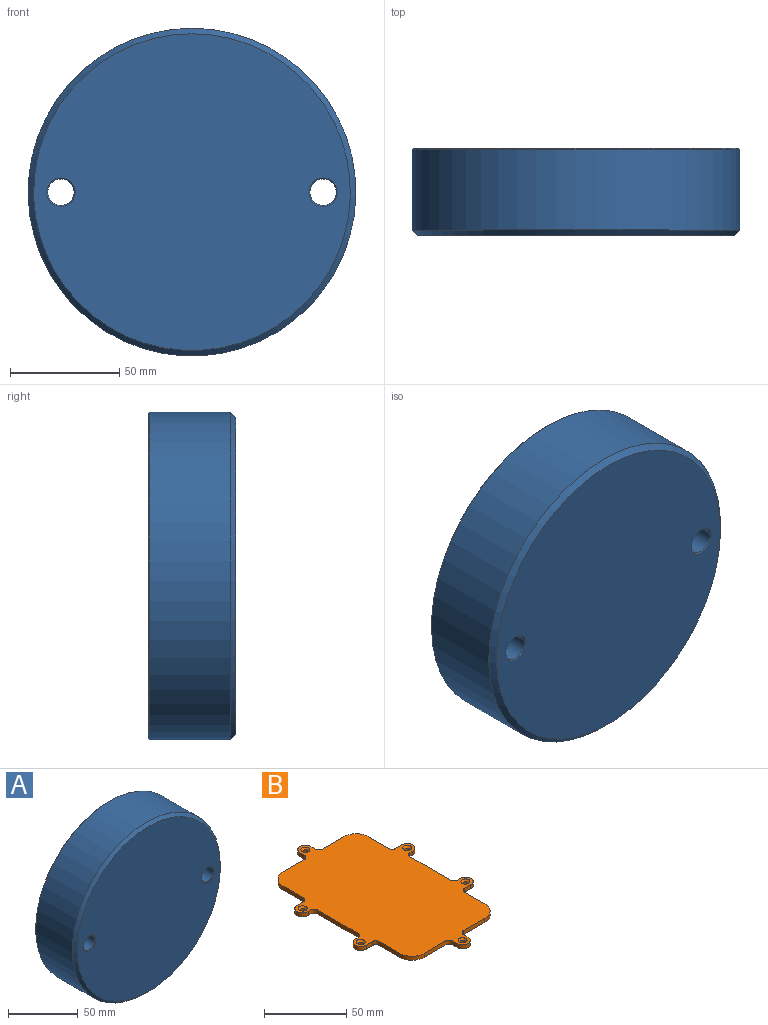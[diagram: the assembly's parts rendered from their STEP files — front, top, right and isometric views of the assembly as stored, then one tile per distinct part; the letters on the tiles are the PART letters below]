
ASSEMBLY  parts=2 mates=1
PART A: 111 faces, bbox 150x40x150 mm
  f0: cone r=75mm half-angle=45deg, axis (0,1,0), area 1638.3mm2, adj f15,f22
  f1: cone r=6mm half-angle=45deg, axis (0,1,0), area 27.8mm2, adj f13,f21
  f2: cone r=6mm half-angle=45deg, axis (0,1,0), area 27.8mm2, adj f14,f21
  f3: cone r=6mm half-angle=45deg, axis (0,-1,0), area 27.8mm2, adj f14,f22
  f4: cone r=6mm half-angle=45deg, axis (0,-1,0), area 27.8mm2, adj f13,f22
  f5: cone r=74.5mm half-angle=45deg, axis (0,-1,0), area 332.1mm2, adj f15,f21
  f6: cylinder r=1.5mm len=16mm, axis (0,1,0), area 150.8mm2, adj f16,f110
  f7: cylinder r=1.5mm len=16mm, axis (0,1,0), area 150.8mm2, adj f17,f109
  f8: cylinder r=1.5mm len=16mm, axis (0,1,0), area 150.8mm2, adj f18,f108
  f9: cylinder r=1.5mm len=16mm, axis (0,1,0), area 150.8mm2, adj f19,f107
  f10: cylinder r=1.5mm len=16mm, axis (0,1,0), area 150.8mm2, adj f20,f106
  f11: cylinder r=1.5mm len=16mm, axis (0,1,0), area 150.8mm2, adj f20,f105
  f12: cylinder r=5mm len=10mm, axis (0,1,0), area 47.1mm2, adj f16,f21,f46,f47
  f13: cylinder r=6mm len=39mm, axis (0,1,0), area 1470.3mm2, adj f1,f4
  f14: cylinder r=6mm len=39mm, axis (0,1,0), area 1470.3mm2, adj f2,f3
  f15: cylinder r=75mm len=150mm, axis (0,-1,0), area 17435.8mm2, adj f0,f5
  f16: plane 15x11.5mm, normal (0,1,0), area 99.9mm2, adj f6,f12,f44,f45,f46,f47,f48
  f17: plane 12.71x11.5mm, normal (0,1,0), area 84.3mm2, adj f7,f51,f52,f53,f54,f55,f56,f79
  f18: plane 15x11.5mm, normal (0,1,0), area 99.9mm2, adj f8,f23,f24,f25,f26,f27,f28
  f19: plane 12.71x11.5mm, normal (0,1,0), area 84.3mm2, adj f9,f56,f57,f58,f59,f60,f61,f80
  f20: plane 62.71x13mm, normal (0,1,0), area 169.1mm2, adj f10,f11,f31,f32,f33,f34,f35,f36
  f21: plane 149x149mm, normal (0,1,0), area 7305.3mm2, adj f1,f2,f5,f12,f23,f24,f25,f26
  f22: plane 145x145mm, normal (0,-1,0), area 16247.5mm2, adj f0,f3,f4
  f23: cylinder r=2.5mm len=3mm, axis (0,1,0), area 11.8mm2, adj f18,f21,f24,f28
  f24: plane 4x3mm, normal (1,0,0), area 12mm2, adj f18,f21,f23,f25
  f25: cylinder r=5mm len=10mm, axis (0,1,0), area 47.1mm2, adj f18,f21,f24,f26
  f26: plane 4x3mm, normal (-1,0,0), area 12mm2, adj f18,f21,f25,f27
  f27: cylinder r=2.5mm len=3mm, axis (0,1,0), area 11.8mm2, adj f18,f21,f26,f28
  f28: plane 52x6mm, normal (0,0,1), area 267mm2, adj f18,f21,f23,f27,f29,f63,f86
  f29: cylinder r=11mm len=11mm, axis (0,1,0), area 103.7mm2, adj f21,f28,f30,f86
  f30: plane 17.5x6mm, normal (-1,0,0), area 105mm2, adj f21,f29,f31,f81,f86
  f31: cylinder r=2.5mm len=3mm, axis (0,1,0), area 11.8mm2, adj f20,f21,f30,f32
  f32: plane 5.5x3mm, normal (0,0,1), area 16.5mm2, adj f20,f21,f31,f33
  f33: cylinder r=5mm len=10mm, axis (0,1,0), area 47.1mm2, adj f20,f21,f32,f34
  f34: plane 3x2.5mm, normal (0,0,-1), area 7.5mm2, adj f20,f21,f33,f35
  f35: cylinder r=2.5mm len=3mm, axis (0,1,0), area 11.8mm2, adj f20,f21,f34,f36
  f36: plane 35x3mm, normal (-1,0,0), area 105mm2, adj f20,f21,f35,f37
  f37: cylinder r=2.5mm len=3mm, axis (0,1,0), area 11.8mm2, adj f20,f21,f36,f38
  f38: plane 3x2.5mm, normal (0,0,1), area 7.5mm2, adj f20,f21,f37,f39
  f39: cylinder r=5mm len=10mm, axis (0,1,0), area 47.1mm2, adj f20,f21,f38,f40
  f40: plane 5.5x3mm, normal (0,0,-1), area 16.5mm2, adj f20,f21,f39,f41
  f41: cylinder r=2.5mm len=6mm, axis (0,1,0), area 20.5mm2, adj f20,f21,f40,f42,f84,f86
  f42: plane 17.5x6mm, normal (-1,0,0), area 105mm2, adj f21,f41,f43,f86
  f43: cylinder r=11mm len=11mm, axis (0,1,0), area 103.7mm2, adj f21,f42,f44,f86
  f44: plane 52x6mm, normal (0,0,-1), area 267mm2, adj f16,f21,f43,f45,f48,f49,f86
  f45: cylinder r=2.5mm len=3mm, axis (0,1,0), area 11.8mm2, adj f16,f21,f44,f46
  f46: plane 4x3mm, normal (-1,0,0), area 12mm2, adj f12,f16,f21,f45
  f47: plane 4x3mm, normal (1,0,0), area 12mm2, adj f12,f16,f21,f48
  f48: cylinder r=2.5mm len=3mm, axis (0,1,0), area 11.8mm2, adj f16,f21,f44,f47
  f49: cylinder r=11mm len=11mm, axis (0,1,0), area 103.7mm2, adj f21,f44,f50,f86
  f50: plane 17.5x6mm, normal (1,0,0), area 105mm2, adj f21,f49,f51,f86
  f51: cylinder r=2.5mm len=6mm, axis (0,1,0), area 20.5mm2, adj f17,f21,f50,f52,f79,f86
  f52: plane 5.5x3mm, normal (0,0,-1), area 16.5mm2, adj f17,f21,f51,f53
  f53: cylinder r=5mm len=10mm, axis (0,1,0), area 47.1mm2, adj f17,f21,f52,f54
  f54: plane 3x2.5mm, normal (0,0,1), area 7.5mm2, adj f17,f21,f53,f55
  f55: cylinder r=2.5mm len=3mm, axis (0,1,0), area 11.8mm2, adj f17,f21,f54,f56
  f56: plane 55.84x6mm, normal (1,0,0), area 272.5mm2, adj f17,f19,f21,f55,f57,f79,f80,f86
  f57: cylinder r=2.5mm len=3mm, axis (0,1,0), area 11.8mm2, adj f19,f21,f56,f58
  f58: plane 3x2.5mm, normal (0,0,-1), area 7.5mm2, adj f19,f21,f57,f59
  f59: cylinder r=5mm len=10mm, axis (0,1,0), area 47.1mm2, adj f19,f21,f58,f60
  f60: plane 5.5x3mm, normal (0,0,1), area 16.5mm2, adj f19,f21,f59,f61
  f61: cylinder r=2.5mm len=6mm, axis (0,1,0), area 20.5mm2, adj f19,f21,f60,f62,f80,f86
  f62: plane 17.5x6mm, normal (1,0,0), area 105mm2, adj f21,f61,f63,f86
  f63: cylinder r=11mm len=11mm, axis (0,1,0), area 103.7mm2, adj f21,f28,f62,f86
  f64: plane 52x3mm, normal (0,0,-1), area 156mm2, adj f65,f85,f86,f104
  f65: cylinder r=7mm len=7mm, axis (0,1,0), area 33mm2, adj f64,f66,f86,f104
  f66: plane 17.5x3mm, normal (-1,0,0), area 52.5mm2, adj f65,f67,f86,f104
  f67: cylinder r=6.5mm len=5.48mm, axis (0,1,0), area 19.5mm2, adj f66,f68,f86,f104
  f68: plane 54.05x3mm, normal (-1,0,0), area 162.1mm2, adj f67,f69,f86,f104
  f69: cylinder r=6.5mm len=5.48mm, axis (0,1,0), area 19.5mm2, adj f68,f70,f86,f104
  f70: plane 17.5x3mm, normal (-1,0,0), area 52.5mm2, adj f69,f71,f86,f104
  f71: cylinder r=7mm len=7mm, axis (0,1,0), area 33mm2, adj f70,f72,f86,f104
  f72: plane 52x3mm, normal (0,0,1), area 156mm2, adj f71,f73,f86,f104
  f73: cylinder r=7mm len=7mm, axis (0,1,0), area 33mm2, adj f72,f74,f86,f104
  f74: plane 17.5x3mm, normal (1,0,0), area 52.5mm2, adj f73,f75,f86,f104
  f75: cylinder r=6.5mm len=5.47mm, axis (0,1,0), area 19.5mm2, adj f74,f76,f86,f104
  f76: plane 54.05x3mm, normal (1,0,0), area 162.2mm2, adj f75,f77,f86,f104
  f77: cylinder r=6.5mm len=5.47mm, axis (0,1,0), area 19.5mm2, adj f76,f78,f86,f104
  f78: plane 17.5x3mm, normal (1,0,0), area 52.5mm2, adj f77,f85,f86,f104
  f79: cylinder r=2.5mm len=3mm, axis (0,1,0), area 8.7mm2, adj f17,f51,f56,f86
  f80: cylinder r=2.5mm len=3mm, axis (0,1,0), area 8.7mm2, adj f19,f56,f61,f86
  f81: cylinder r=2.5mm len=3mm, axis (0,1,0), area 8.7mm2, adj f20,f30,f82,f86
  f82: cylinder r=2.5mm len=3mm, axis (0,1,0), area 8.7mm2, adj f20,f81,f83,f86
  f83: plane 55.84x3mm, normal (-1,0,0), area 167.5mm2, adj f20,f82,f84,f86
  f84: cylinder r=2.5mm len=3mm, axis (0,1,0), area 8.7mm2, adj f20,f41,f83,f86
  f85: cylinder r=7mm len=7mm, axis (0,1,0), area 33mm2, adj f64,f78,f86,f104
  f86: plane 122x79.99mm, normal (0,1,0), area 1461mm2, adj f28,f29,f30,f41,f42,f43,f44,f49
  f87: plane 110x68mm, normal (0,1,0), area 7072.2mm2, adj f88,f89,f90,f91,f92,f93,f94,f95
  f88: cylinder r=5mm len=34mm, axis (0,1,0), area 267mm2, adj f87,f89,f103,f104
  f89: plane 34x25.92mm, normal (-1,0,0), area 881.2mm2, adj f87,f88,f90,f104
  f90: cylinder r=5mm len=34mm, axis (0,1,0), area 197.1mm2, adj f87,f89,f91,f104
  f91: plane 39x34mm, normal (-1,0,0), area 1326mm2, adj f87,f90,f92,f104
  f92: cylinder r=5mm len=34mm, axis (0,1,0), area 197.1mm2, adj f87,f91,f93,f104
  f93: plane 34x25.92mm, normal (-1,0,0), area 881.2mm2, adj f87,f92,f94,f104
  f94: cylinder r=5mm len=34mm, axis (0,1,0), area 267mm2, adj f87,f93,f95,f104
  f95: plane 52x34mm, normal (0,0,1), area 1768mm2, adj f87,f94,f96,f104
  f96: cylinder r=5mm len=34mm, axis (0,1,0), area 267mm2, adj f87,f95,f97,f104
  f97: plane 34x25.92mm, normal (1,0,0), area 881.2mm2, adj f87,f96,f98,f104
  f98: cylinder r=5mm len=34mm, axis (0,1,0), area 197.1mm2, adj f87,f97,f99,f104
  f99: plane 39x34mm, normal (1,0,0), area 1326mm2, adj f87,f98,f100,f104
  f100: cylinder r=5mm len=34mm, axis (0,1,0), area 197.1mm2, adj f87,f99,f101,f104
  f101: plane 34x25.92mm, normal (1,0,0), area 881.2mm2, adj f87,f100,f102,f104
  f102: cylinder r=5mm len=34mm, axis (0,1,0), area 267mm2, adj f87,f101,f103,f104
  f103: plane 52x34mm, normal (0,0,-1), area 1768mm2, adj f87,f88,f102,f104
  f104: plane 114x71.99mm, normal (0,1,0), area 752.8mm2, adj f64,f65,f66,f67,f68,f69,f70,f71
  f105: plane 3x3mm, normal (0,1,0), area 7.1mm2, adj f11
  f106: plane 3x3mm, normal (0,1,0), area 7.1mm2, adj f10
  f107: plane 3x3mm, normal (0,1,0), area 7.1mm2, adj f9
  f108: plane 3x3mm, normal (0,1,0), area 7.1mm2, adj f8
  f109: plane 3x3mm, normal (0,1,0), area 7.1mm2, adj f7
  f110: plane 3x3mm, normal (0,1,0), area 7.1mm2, adj f6
PART B: 58 faces, bbox 99.4x144.4x3 mm
  f0: cone r=2.75mm half-angle=45deg, axis (0,0,1), area 23.6mm2, adj f8,f14
  f1: cone r=2.75mm half-angle=45deg, axis (0,0,1), area 23.6mm2, adj f7,f14
  f2: cone r=2.75mm half-angle=45deg, axis (0,0,1), area 23.6mm2, adj f6,f14
  f3: cone r=2.75mm half-angle=45deg, axis (0,0,1), area 23.6mm2, adj f11,f14
  f4: cone r=2.75mm half-angle=45deg, axis (0,0,1), area 23.6mm2, adj f10,f14
  f5: cone r=2.75mm half-angle=45deg, axis (0,0,1), area 23.6mm2, adj f9,f14
  f6: cylinder r=1.5mm len=3mm, axis (0,0,-1), area 16.5mm2, adj f2,f15
  f7: cylinder r=1.5mm len=3mm, axis (0,0,-1), area 16.5mm2, adj f1,f15
  f8: cylinder r=1.5mm len=3mm, axis (0,0,-1), area 16.5mm2, adj f0,f15
  f9: cylinder r=1.5mm len=3mm, axis (0,0,-1), area 16.5mm2, adj f5,f15
  f10: cylinder r=1.5mm len=3mm, axis (0,0,-1), area 16.5mm2, adj f4,f15
  f11: cylinder r=1.5mm len=3mm, axis (0,0,-1), area 16.5mm2, adj f3,f15
  f12: cylinder r=4.7mm len=9.4mm, axis (0,0,-1), area 44.3mm2, adj f14,f15,f26,f27
  f13: cylinder r=4.7mm len=9.4mm, axis (0,0,-1), area 44.3mm2, adj f14,f15,f21,f22
  f14: plane 144.4x99.4mm, normal (0,0,1), area 9581.8mm2, adj f0,f1,f2,f3,f4,f5,f12,f13
  f15: plane 144.4x99.4mm, normal (0,0,-1), area 9682mm2, adj f6,f7,f8,f9,f10,f11,f12,f13
  f16: cylinder r=2.8mm len=3mm, axis (0,0,-1), area 13.2mm2, adj f14,f15,f17,f57
  f17: plane 18.5x3mm, normal (0,1,0), area 55.5mm2, adj f14,f15,f16,f18
  f18: cylinder r=10.7mm len=10.7mm, axis (0,0,-1), area 50.4mm2, adj f14,f15,f17,f19
  f19: plane 17.5x3mm, normal (-1,0,0), area 52.5mm2, adj f14,f15,f18,f20
  f20: cylinder r=2.8mm len=3mm, axis (0,0,-1), area 13.2mm2, adj f14,f15,f19,f21
  f21: plane 5.5x3mm, normal (0,1,0), area 16.5mm2, adj f13,f14,f15,f20
  f22: plane 3x2.5mm, normal (0,-1,0), area 7.5mm2, adj f13,f14,f15,f23
  f23: cylinder r=2.8mm len=3mm, axis (0,0,-1), area 13.2mm2, adj f14,f15,f22,f24
  f24: plane 35x3mm, normal (-1,0,0), area 105mm2, adj f14,f15,f23,f25
  f25: cylinder r=2.8mm len=3mm, axis (0,0,-1), area 13.2mm2, adj f14,f15,f24,f26
  f26: plane 3x2.5mm, normal (0,1,0), area 7.5mm2, adj f12,f14,f15,f25
  f27: plane 5.5x3mm, normal (0,-1,0), area 16.5mm2, adj f12,f14,f15,f28
  f28: cylinder r=2.8mm len=3mm, axis (0,0,-1), area 13.2mm2, adj f14,f15,f27,f29
  f29: plane 17.5x3mm, normal (-1,0,0), area 52.5mm2, adj f14,f15,f28,f30
  f30: cylinder r=10.7mm len=10.7mm, axis (0,0,-1), area 50.4mm2, adj f14,f15,f29,f31
  f31: plane 18.5x3mm, normal (0,-1,0), area 55.5mm2, adj f14,f15,f30,f32
  f32: cylinder r=2.8mm len=3mm, axis (0,0,-1), area 13.2mm2, adj f14,f15,f31,f33
  f33: plane 4x3mm, normal (-1,0,0), area 12mm2, adj f14,f15,f32,f34
  f34: cylinder r=4.7mm len=9.4mm, axis (0,0,-1), area 44.3mm2, adj f14,f15,f33,f35
  f35: plane 4x3mm, normal (1,0,0), area 12mm2, adj f14,f15,f34,f36
  f36: cylinder r=2.8mm len=3mm, axis (0,0,-1), area 13.2mm2, adj f14,f15,f35,f37
  f37: plane 18.5x3mm, normal (0,-1,0), area 55.5mm2, adj f14,f15,f36,f38
  f38: cylinder r=10.7mm len=10.7mm, axis (0,0,-1), area 50.4mm2, adj f14,f15,f37,f39
  f39: plane 17.5x3mm, normal (1,0,0), area 52.5mm2, adj f14,f15,f38,f40
  f40: cylinder r=2.8mm len=3mm, axis (0,0,-1), area 13.2mm2, adj f14,f15,f39,f41
  f41: plane 5.5x3mm, normal (0,-1,0), area 16.5mm2, adj f14,f15,f40,f42
  f42: cylinder r=4.7mm len=9.4mm, axis (0,0,-1), area 44.3mm2, adj f14,f15,f41,f43
  f43: plane 3x2.5mm, normal (0,1,0), area 7.5mm2, adj f14,f15,f42,f44
  f44: cylinder r=2.8mm len=3mm, axis (0,0,-1), area 13.2mm2, adj f14,f15,f43,f45
  f45: plane 35x3mm, normal (1,0,0), area 105mm2, adj f14,f15,f44,f46
  f46: cylinder r=2.8mm len=3mm, axis (0,0,-1), area 13.2mm2, adj f14,f15,f45,f47
  f47: plane 3x2.5mm, normal (0,-1,0), area 7.5mm2, adj f14,f15,f46,f48
  f48: cylinder r=4.7mm len=9.4mm, axis (0,0,-1), area 44.3mm2, adj f14,f15,f47,f49
  f49: plane 5.5x3mm, normal (0,1,0), area 16.5mm2, adj f14,f15,f48,f50
  f50: cylinder r=2.8mm len=3mm, axis (0,0,-1), area 13.2mm2, adj f14,f15,f49,f51
  f51: plane 17.5x3mm, normal (1,0,0), area 52.5mm2, adj f14,f15,f50,f52
  f52: cylinder r=10.7mm len=10.7mm, axis (0,0,-1), area 50.4mm2, adj f14,f15,f51,f53
  f53: plane 18.5x3mm, normal (0,1,0), area 55.5mm2, adj f14,f15,f52,f54
  f54: cylinder r=2.8mm len=3mm, axis (0,0,-1), area 13.2mm2, adj f14,f15,f53,f55
  f55: plane 4x3mm, normal (1,0,0), area 12mm2, adj f14,f15,f54,f56
  f56: cylinder r=4.7mm len=9.4mm, axis (0,0,-1), area 44.3mm2, adj f14,f15,f55,f57
  f57: plane 4x3mm, normal (-1,0,0), area 12mm2, adj f14,f15,f16,f56
PLACE A t=(1.73,7.11,4.67)mm
PLACE B rot(axis=(-1,0,0),90deg) t=(1.73,44.11,4.67)mm
MATE fastened A.f8 <-> B.f5  axis (0,1,0) through (1.73,44.11,-62.83)mm
